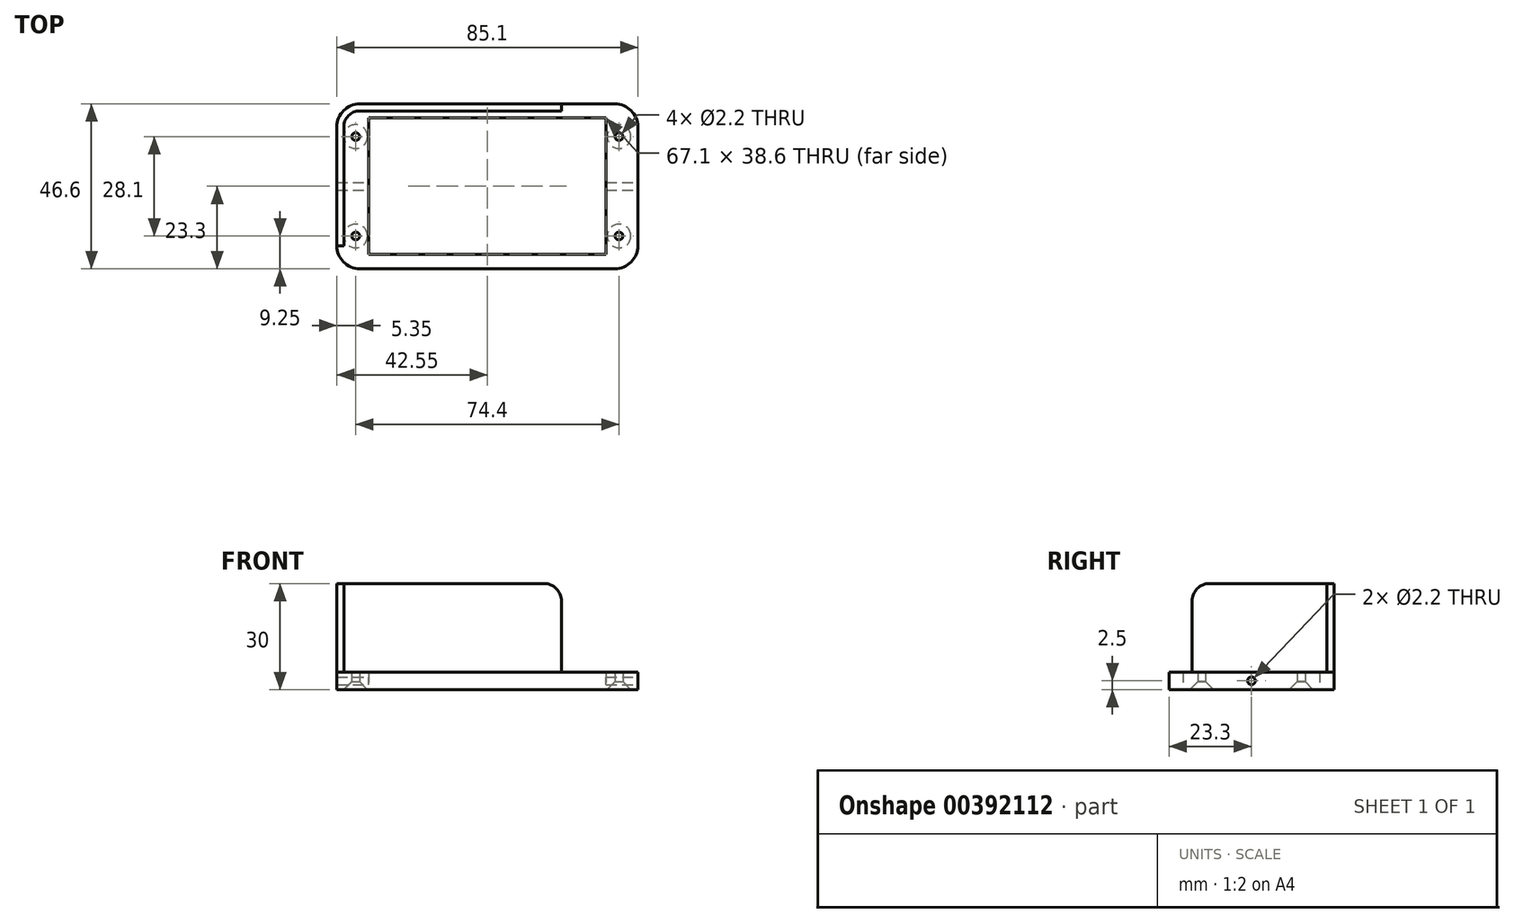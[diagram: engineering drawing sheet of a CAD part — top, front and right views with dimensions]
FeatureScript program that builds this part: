
annotation { "Feature Type Name" : "Feature", "Feature Type Description" : "" }
export const myFeature = defineFeature(function(context is Context, id is Id, definition is map)
    precondition{}
    {
        {
            var Q0;
            Q0=qCreatedBy(makeId("Top.planeOp"),FACE);
            var sketch = newSketch(context, id + "F0", { "sketchPlane" : qUnion([Q0])});
            skLineSegment(sketch, "E0.bottom", {"start": v(36.05, 21.3) * mm, "end": v(-36.05, 21.3) * mm});
            skLineSegment(sketch, "E0.top", {"start": v(36.05, -21.3) * mm, "end": v(-36.05, -21.3) * mm});
            skLineSegment(sketch, "E0.left", {"start": v(40.55, 16.8) * mm, "end": v(40.55, -16.8) * mm});
            skLineSegment(sketch, "E0.right", {"start": v(-40.55, 16.8) * mm, "end": v(-40.55, -16.8) * mm});
            skPoint(sketch, "E0.middle", {"position": v(0, 0) * mm});
            skArc(sketch, "E1.filletArc", {"start": v(-36.05, 21.3) * mm, "mid": v(-39.23, 19.98) * mm, "end": v(-40.55, 16.8) * mm});
            skPoint(sketch, "E2.visualSharp", {"position": v(40.55, 21.3) * mm});
            skArc(sketch, "E2.filletArc", {"start": v(40.55, 16.8) * mm, "mid": v(39.23, 19.98) * mm, "end": v(36.05, 21.3) * mm});
            skPoint(sketch, "E3.visualSharp", {"position": v(40.55, -21.3) * mm});
            skArc(sketch, "E3.filletArc", {"start": v(36.05, -21.3) * mm, "mid": v(39.23, -19.98) * mm, "end": v(40.55, -16.8) * mm});
            skPoint(sketch, "E4.visualSharp", {"position": v(-40.55, -21.3) * mm});
            skArc(sketch, "E4.filletArc", {"start": v(-40.55, -16.8) * mm, "mid": v(-39.23, -19.98) * mm, "end": v(-36.05, -21.3) * mm});
            skLineSegment(sketch, "E5", {"start": v(40.55, 0) * mm, "end": v(-40.55, 0) * mm, "construction": true});
            skLineSegment(sketch, "E6", {"start": v(0, 21.3) * mm, "end": v(0, -21.3) * mm, "construction": true});
            skLineSegment(sketch, "E7.bottom", {"start": v(-37.2, 14.05) * mm, "end": v(37.2, 14.05) * mm, "construction": true});
            skLineSegment(sketch, "E7.top", {"start": v(-37.2, -14.05) * mm, "end": v(37.2, -14.05) * mm, "construction": true});
            skLineSegment(sketch, "E7.left", {"start": v(-37.2, 14.05) * mm, "end": v(-37.2, -14.05) * mm, "construction": true});
            skLineSegment(sketch, "E7.right", {"start": v(37.2, 14.05) * mm, "end": v(37.2, -14.05) * mm, "construction": true});
            skPoint(sketch, "E8", {"position": v(37.2, 14.05) * mm});
            skPoint(sketch, "E9", {"position": v(37.2, -14.05) * mm});
            skPoint(sketch, "E10", {"position": v(-37.2, -14.05) * mm});
            skPoint(sketch, "E11", {"position": v(-37.2, 14.05) * mm});
            skArc(sketch, "E12.0", {"start": v(42.55, 16.8) * mm, "mid": v(40.65, 21.4) * mm, "end": v(36.05, 23.3) * mm});
            skLineSegment(sketch, "E12.1", {"start": v(42.55, 16.8) * mm, "end": v(42.55, -16.8) * mm});
            skLineSegment(sketch, "E12.2", {"start": v(36.05, 23.3) * mm, "end": v(-36.05, 23.3) * mm});
            skArc(sketch, "E12.3", {"start": v(36.05, -23.3) * mm, "mid": v(40.65, -21.4) * mm, "end": v(42.55, -16.8) * mm});
            skArc(sketch, "E12.4", {"start": v(-36.05, 23.3) * mm, "mid": v(-40.65, 21.4) * mm, "end": v(-42.55, 16.8) * mm});
            skLineSegment(sketch, "E12.5", {"start": v(-42.55, 16.8) * mm, "end": v(-42.55, -16.8) * mm});
            skArc(sketch, "E12.6", {"start": v(-42.55, -16.8) * mm, "mid": v(-40.65, -21.4) * mm, "end": v(-36.05, -23.3) * mm});
            skLineSegment(sketch, "E12.7", {"start": v(36.05, -23.3) * mm, "end": v(-36.05, -23.3) * mm});
            skLineSegment(sketch, "E13.bottom", {"start": v(33.55, 19.3) * mm, "end": v(-33.55, 19.3) * mm});
            skLineSegment(sketch, "E13.top", {"start": v(33.55, -19.3) * mm, "end": v(-33.55, -19.3) * mm});
            skLineSegment(sketch, "E13.left", {"start": v(33.55, 19.3) * mm, "end": v(33.55, -19.3) * mm});
            skLineSegment(sketch, "E13.right", {"start": v(-33.55, 19.3) * mm, "end": v(-33.55, -19.3) * mm});
            skLineSegment(sketch, "E14.bottom", {"start": v(-11.05, 8) * mm, "end": v(-25.55, 8) * mm, "construction": true});
            skLineSegment(sketch, "E14.top", {"start": v(-11.05, -8) * mm, "end": v(-25.55, -8) * mm, "construction": true});
            skLineSegment(sketch, "E14.left", {"start": v(-11.05, 8) * mm, "end": v(-11.05, -8) * mm, "construction": true});
            skLineSegment(sketch, "E14.right", {"start": v(-25.55, 8) * mm, "end": v(-25.55, -8) * mm, "construction": true});
            skPoint(sketch, "E14.middle", {"position": v(-18.3, 0) * mm});
            skLineSegment(sketch, "E15", {"start": v(42.55, 16.8) * mm, "end": v(40.55, 16.8) * mm});
            skLineSegment(sketch, "E16", {"start": v(-14.45, -23.3) * mm, "end": v(-14.45, -21.3) * mm});
            skSolve(sketch);
        }
        {
            var Q0;
            Q0=makeQuery(id+"F0.imprint","IMPRINT",FACE,{"disambiguationData":[TD([[makeQuery(id+"F0.imprint","IMPRINT",EDGE,{"derivedFrom":sQuery(id+"F0.wireOp",EDGE,"E0.bottom")}),1.0]])]});
            extrude(context, id + "F1", {"entities" : qUnion([Q0]), "depth" : 5 * mm});
        }
        {
            var Q0;
            Q0=qSketchRegion(id+"F0",true);
            extrude(context, id + "F2", {"entities" : qUnion([Q0]), "operationType" : NewBodyOperationType.ADD, "depth" : 5 * mm});
        }
        {
            var Q0;
            Q0=sQuery(id+"F0.wireOp",VERTEX,"E8");
            var Q1;
            Q1=sQuery(id+"F0.wireOp",VERTEX,"E9");
            var Q2;
            Q2=sQuery(id+"F0.wireOp",VERTEX,"E10");
            var Q3;
            Q3=sQuery(id+"F0.wireOp",VERTEX,"E11");
            var Q4;
            Q4=makeQuery(id+"F1.opExtrude","SWEPT_BODY",BODY,{"disambiguationData":[OSD([sQuery(id+"F0.wireOp",EDGE,"E0.bottom"),sQuery(id+"F0.wireOp",EDGE,"E0.top"),sQuery(id+"F0.wireOp",EDGE,"E0.left"),sQuery(id+"F0.wireOp",EDGE,"E0.right"),sQuery(id+"F0.wireOp",EDGE,"E1.filletArc"),sQuery(id+"F0.wireOp",EDGE,"E2.filletArc"),sQuery(id+"F0.wireOp",EDGE,"E3.filletArc"),sQuery(id+"F0.wireOp",EDGE,"E4.filletArc"),sQuery(id+"F0.wireOp",EDGE,"E13.bottom"),sQuery(id+"F0.wireOp",EDGE,"E13.top"),sQuery(id+"F0.wireOp",EDGE,"E13.left"),sQuery(id+"F0.wireOp",EDGE,"E13.right")])]});
            hole(context, id + "F3", {"style" : HoleStyle.C_SINK, "endStyle" : HoleEndStyle.THROUGH, "oppositeDirection" : true, "holeDiameter" : 2.2 * mm, "cSinkDiameter" : 6.72 * mm, "cSinkAngle" : 90 * degree, "isTappedThrough" : true, "tappedDepth" : 4 * mm, "tapClearance" : 0, "locations" : qUnion([Q0, Q1, Q2, Q3]), "scope" : qUnion([Q4])});
        }
        {
            var Q0;
            Q0=makeQuery(id+"F2.opExtrude","SWEPT_FACE",FACE,{"disambiguationData":[OSD([sQuery(id+"F0.wireOp",EDGE,"E12.1")])]});
            var sketch = newSketch(context, id + "F4", { "sketchPlane" : qUnion([Q0])});
            skLineSegment(sketch, "E17", {"start": v(0, 5) * mm, "end": v(0, 0) * mm, "construction": true});
            skPoint(sketch, "E18", {"position": v(0, 2.5) * mm});
            skSolve(sketch);
        }
        {
            var Q0;
            Q0=sQuery(id+"F4.wireOp",VERTEX,"E18");
            var Q1;
            Q1=makeQuery(id+"F1.opExtrude","SWEPT_BODY",BODY,{"disambiguationData":[OSD([sQuery(id+"F0.wireOp",EDGE,"E0.bottom"),sQuery(id+"F0.wireOp",EDGE,"E0.top"),sQuery(id+"F0.wireOp",EDGE,"E0.left"),sQuery(id+"F0.wireOp",EDGE,"E0.right"),sQuery(id+"F0.wireOp",EDGE,"E1.filletArc"),sQuery(id+"F0.wireOp",EDGE,"E2.filletArc"),sQuery(id+"F0.wireOp",EDGE,"E3.filletArc"),sQuery(id+"F0.wireOp",EDGE,"E4.filletArc"),sQuery(id+"F0.wireOp",EDGE,"E13.bottom"),sQuery(id+"F0.wireOp",EDGE,"E13.top"),sQuery(id+"F0.wireOp",EDGE,"E13.left"),sQuery(id+"F0.wireOp",EDGE,"E13.right")])]});
            hole(context, id + "F5", {"style" : HoleStyle.SIMPLE, "endStyle" : HoleEndStyle.THROUGH, "holeDiameter" : 2.2 * mm, "isTappedThrough" : true, "tappedDepth" : 4 * mm, "tapClearance" : 0, "locations" : qUnion([Q0]), "scope" : qUnion([Q1])});
        }
        {
            var Q0;
            {var subQ0=sQuery(id+"F0.wireOp",EDGE,"E4.filletArc");var subQ1=sQuery(id+"F0.wireOp",EDGE,"E3.filletArc");var subQ2=sQuery(id+"F0.wireOp",EDGE,"E2.filletArc");var subQ3=sQuery(id+"F0.wireOp",EDGE,"E1.filletArc");var subQ4=sQuery(id+"F0.wireOp",EDGE,"E0.right");var subQ5=sQuery(id+"F0.wireOp",EDGE,"E0.left");var subQ6=sQuery(id+"F0.wireOp",EDGE,"E0.top");var subQ7=sQuery(id+"F0.wireOp",EDGE,"E0.bottom");Q0=makeQuery(id+"F2.boolean.opBoolean","MERGE",FACE,{"derivedFrom":[makeQuery(id+"F1.opExtrude","CAP_FACE",FACE,{"disambiguationData":[OSD([subQ7,subQ6,subQ5,subQ4,subQ3,subQ2,subQ1,subQ0,sQuery(id+"F0.wireOp",EDGE,"E13.bottom"),sQuery(id+"F0.wireOp",EDGE,"E13.top"),sQuery(id+"F0.wireOp",EDGE,"E13.left"),sQuery(id+"F0.wireOp",EDGE,"E13.right")])],"isStart":false}),makeQuery(id+"F2.opExtrude","CAP_FACE",FACE,{"disambiguationData":[OSD([subQ7,subQ6,subQ5,subQ4,subQ3,subQ2,subQ1,subQ0,sQuery(id+"F0.wireOp",EDGE,"E12.0"),sQuery(id+"F0.wireOp",EDGE,"E12.1"),sQuery(id+"F0.wireOp",EDGE,"E12.2"),sQuery(id+"F0.wireOp",EDGE,"E12.3"),sQuery(id+"F0.wireOp",EDGE,"E12.4"),sQuery(id+"F0.wireOp",EDGE,"E12.5"),sQuery(id+"F0.wireOp",EDGE,"E12.6"),sQuery(id+"F0.wireOp",EDGE,"E12.7")])],"isStart":false})]});}
            var sketch = newSketch(context, id + "F6", { "sketchPlane" : qUnion([Q0])});
            skLineSegment(sketch, "E19", {"start": v(-42.55, -16.8) * mm, "end": v(-42.55, 16.8) * mm});
            skLineSegment(sketch, "E20", {"start": v(-36.05, 23.3) * mm, "end": v(20.95, 23.3) * mm});
            skLineSegment(sketch, "E21.0", {"start": v(-36.05, 21.3) * mm, "end": v(20.95, 21.3) * mm});
            skArc(sketch, "E21.1", {"start": v(-36.05, 21.3) * mm, "mid": v(-39.23, 19.98) * mm, "end": v(-40.55, 16.8) * mm});
            skLineSegment(sketch, "E21.2", {"start": v(-40.55, 16.8) * mm, "end": v(-40.55, -16.8) * mm});
            skLineSegment(sketch, "E22", {"start": v(-40.55, -16.8) * mm, "end": v(-42.55, -16.8) * mm});
            skLineSegment(sketch, "E23", {"start": v(20.95, 23.3) * mm, "end": v(20.95, 21.3) * mm});
            skSolve(sketch);
        }
        {
            var Q0;
            Q0=makeQuery(id+"F6.imprint","IMPRINT",FACE,{"disambiguationData":[TD([[makeQuery(id+"F6.imprint","IMPRINT",EDGE,{"derivedFrom":sQuery(id+"F6.wireOp",EDGE,"E19")}),1.0]])]});
            extrude(context, id + "F7", {"entities" : qUnion([Q0]), "operationType" : NewBodyOperationType.ADD, "depth" : 25 * mm});
        }
        {
            var Q0;
            Q0=makeQuery(id+"F7.opExtrude","CAP_EDGE",EDGE,{"disambiguationData":[OSD([sQuery(id+"F6.wireOp",EDGE,"E22")])],"isStart":false});
            var Q1;
            Q1=makeQuery(id+"F7.opExtrude","CAP_EDGE",EDGE,{"disambiguationData":[OSD([sQuery(id+"F6.wireOp",EDGE,"E23")])],"isStart":false});
            var Q2;
            Q2=makeQuery(id+"F7.opExtrude","CAP_EDGE",EDGE,{"disambiguationData":[OSD([sQuery(id+"F6.wireOp",EDGE,"E23")])],"isStart":true});
            fillet(context, id + "F8", {"entities" : qUnion([Q0, Q1, Q2]), "radius" : 5 * mm, "tangentPropagation" : true, "allowEdgeOverflow" : false});
        }
    });
